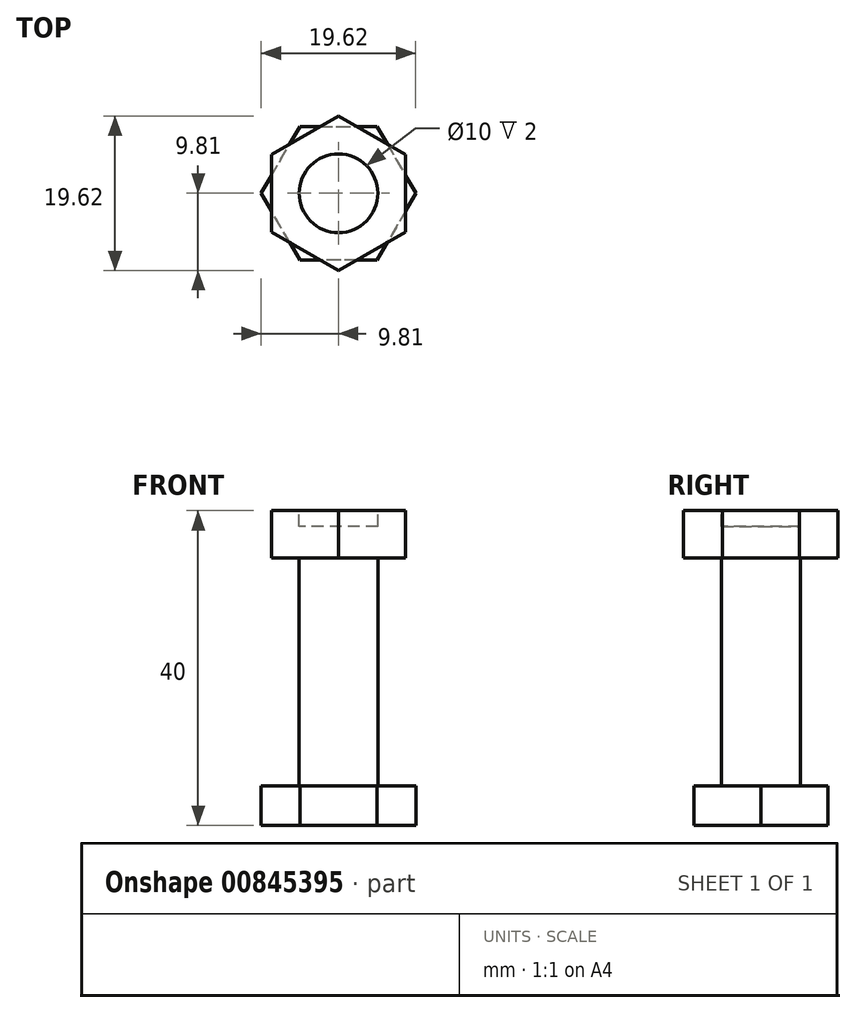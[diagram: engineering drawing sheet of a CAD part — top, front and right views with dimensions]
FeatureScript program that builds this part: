
annotation { "Feature Type Name" : "Feature", "Feature Type Description" : "" }
export const myFeature = defineFeature(function(context is Context, id is Id, definition is map)
    precondition{}
    {
        {
            var Q0;
            Q0=qCreatedBy(makeId("Top.planeOp"),FACE);
            var sketch = newSketch(context, id + "F0", { "sketchPlane" : qUnion([Q0])});
            skCircle(sketch, "E0.cCircle", {"center": v(0, 0) * mm, "radius": 8.5 * mm, "construction": true});
            skLineSegment(sketch, "E0.0", {"start": v(-4.9, 8.5) * mm, "end": v(4.9, 8.5) * mm});
            skLineSegment(sketch, "E0.1", {"start": v(4.9, 8.5) * mm, "end": v(9.81, 0) * mm});
            skLineSegment(sketch, "E0.2", {"start": v(9.81, 0) * mm, "end": v(4.9, -8.5) * mm});
            skLineSegment(sketch, "E0.3", {"start": v(4.9, -8.5) * mm, "end": v(-4.9, -8.5) * mm});
            skLineSegment(sketch, "E0.4", {"start": v(-4.9, -8.5) * mm, "end": v(-9.81, 0) * mm});
            skLineSegment(sketch, "E0.5", {"start": v(-9.81, 0) * mm, "end": v(-4.9, 8.5) * mm});
            skPoint(sketch, "E0.0.midPoint", {"position": v(0, 8.5) * mm});
            skSolve(sketch);
        }
        {
            var Q0;
            Q0=makeQuery(id+"F0.imprint","IMPRINT",FACE,{"disambiguationData":[TD([[makeQuery(id+"F0.imprint","IMPRINT",EDGE,{"derivedFrom":sQuery(id+"F0.wireOp",EDGE,"E0.0")}),-1.0]])]});
            extrude(context, id + "F1", {"entities" : qUnion([Q0]), "depth" : 5 * mm, "offsetDistance" : 25 * mm});
        }
        {
            var Q0;
            Q0=makeQuery(id+"F1.opExtrude","CAP_FACE",FACE,{"disambiguationData":[OSD([sQuery(id+"F0.wireOp",EDGE,"E0.0"),sQuery(id+"F0.wireOp",EDGE,"E0.1"),sQuery(id+"F0.wireOp",EDGE,"E0.2"),sQuery(id+"F0.wireOp",EDGE,"E0.3"),sQuery(id+"F0.wireOp",EDGE,"E0.4"),sQuery(id+"F0.wireOp",EDGE,"E0.5")])],"isStart":false});
            var sketch = newSketch(context, id + "F2", { "sketchPlane" : qUnion([Q0])});
            skCircle(sketch, "E1", {"center": v(0, 0) * mm, "radius": 5 * mm});
            skSolve(sketch);
        }
        {
            var Q0;
            Q0=makeQuery(id+"F2.imprint","IMPRINT",FACE,{"disambiguationData":[TD([[makeQuery(id+"F2.imprint","IMPRINT",EDGE,{"derivedFrom":sQuery(id+"F2.wireOp",EDGE,"E1")}),1.0]])]});
            extrude(context, id + "F3", {"entities" : qUnion([Q0]), "operationType" : NewBodyOperationType.ADD, "depth" : 35 * mm, "offsetDistance" : 25 * mm});
        }
        {
            var Q0;
            Q0=makeQuery(id+"F3.opExtrude","CAP_FACE",FACE,{"disambiguationData":[OSD([sQuery(id+"F2.wireOp",EDGE,"E1")])],"isStart":false});
            var sketch = newSketch(context, id + "F4", { "sketchPlane" : qUnion([Q0])});
            skCircle(sketch, "E2.cCircle", {"center": v(0, 0) * mm, "radius": 8.5 * mm, "construction": true});
            skLineSegment(sketch, "E2.0", {"start": v(-8.5, -4.9) * mm, "end": v(-8.5, 4.9) * mm});
            skLineSegment(sketch, "E2.1", {"start": v(-8.5, 4.9) * mm, "end": v(0, 9.81) * mm});
            skLineSegment(sketch, "E2.2", {"start": v(0, 9.81) * mm, "end": v(8.5, 4.9) * mm});
            skLineSegment(sketch, "E2.3", {"start": v(8.5, 4.9) * mm, "end": v(8.5, -4.9) * mm});
            skLineSegment(sketch, "E2.4", {"start": v(8.5, -4.9) * mm, "end": v(0, -9.81) * mm});
            skLineSegment(sketch, "E2.5", {"start": v(0, -9.81) * mm, "end": v(-8.5, -4.9) * mm});
            skPoint(sketch, "E2.0.midPoint", {"position": v(-8.5, 0) * mm});
            skSolve(sketch);
        }
        {
            var Q0;
            Q0=makeQuery(id+"F4.imprint","IMPRINT",FACE,{"disambiguationData":[TD([[makeQuery(id+"F4.imprint","IMPRINT",EDGE,{"derivedFrom":sQuery(id+"F4.wireOp",EDGE,"E2.0")}),-1.0]])]});
            extrude(context, id + "F5", {"entities" : qUnion([Q0]), "operationType" : NewBodyOperationType.ADD, "oppositeDirection" : true, "depth" : 6 * mm, "offsetDistance" : 25 * mm});
        }
        {
            var Q0;
            {var subQ0=sQuery(id+"F2.wireOp",EDGE,"E1");Q0=makeQuery(id+"F5.boolean.opBoolean","MERGE",FACE,{"derivedFrom":[makeQuery(id+"F3.opExtrude","CAP_FACE",FACE,{"disambiguationData":[OSD([subQ0])],"isStart":false}),makeQuery(id+"F5.opExtrude","CAP_FACE",FACE,{"disambiguationData":[OSD([subQ0,sQuery(id+"F4.wireOp",EDGE,"E2.0"),sQuery(id+"F4.wireOp",EDGE,"E2.1"),sQuery(id+"F4.wireOp",EDGE,"E2.2"),sQuery(id+"F4.wireOp",EDGE,"E2.3"),sQuery(id+"F4.wireOp",EDGE,"E2.4"),sQuery(id+"F4.wireOp",EDGE,"E2.5")])],"isStart":true})]});}
            var sketch = newSketch(context, id + "F6", { "sketchPlane" : qUnion([Q0])});
            skCircle(sketch, "E3", {"center": v(0, 0) * mm, "radius": 5 * mm});
            skSolve(sketch);
        }
        {
            var Q0;
            Q0=makeQuery(id+"F6.imprint","IMPRINT",FACE,{"disambiguationData":[TD([[makeQuery(id+"F6.imprint","IMPRINT",EDGE,{"derivedFrom":sQuery(id+"F6.wireOp",EDGE,"E3")}),1.0]])]});
            extrude(context, id + "F7", {"entities" : qUnion([Q0]), "operationType" : NewBodyOperationType.REMOVE, "oppositeDirection" : true, "depth" : 2 * mm, "offsetDistance" : 25 * mm});
        }
    });
